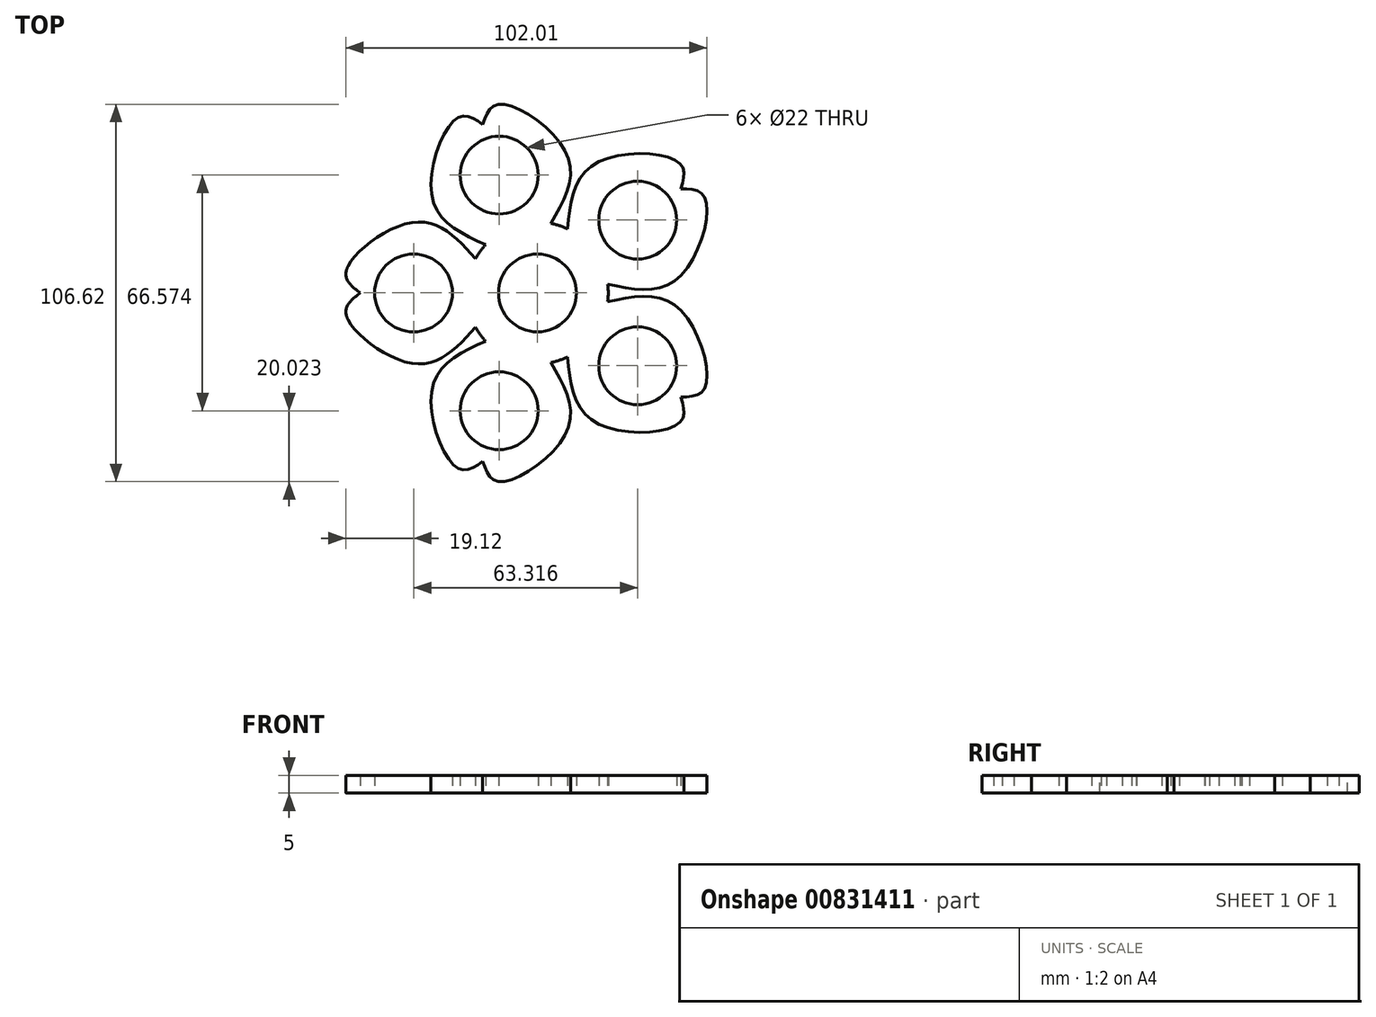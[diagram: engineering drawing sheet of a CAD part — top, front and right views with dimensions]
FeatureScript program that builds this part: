
annotation { "Feature Type Name" : "Feature", "Feature Type Description" : "" }
export const myFeature = defineFeature(function(context is Context, id is Id, definition is map)
    precondition{}
    {
        {
            var Q0;
            Q0=qCreatedBy(makeId("Top.planeOp"),FACE);
            var sketch = newSketch(context, id + "F0", { "sketchPlane" : qUnion([Q0])});
            skCircle(sketch, "E0", {"center": v(0, 0) * mm, "radius": 11 * mm});
            skArc(sketch, "E1", {"start": v(-17.5, -9.68) * mm, "mid": v(-16.18, -11.76) * mm, "end": v(-14.62, -13.65) * mm});
            skCircle(sketch, "E2", {"center": v(-35, 0) * mm, "radius": 11 * mm});
            skFitSpline(sketch, "E3", {"points": [v(-17.5, 9.68) * mm, v(-34.6, 20) * mm, v(-54.02, 6.18) * mm, v(-50.04, 0) * mm], "startDerivative": vector(-40.19, 44.56) * mm, "endDerivative": vector(30.5, -23.06) * mm});
            skArc(sketch, "E4.trimOffspring", {"start": v(-53.51, 7.57) * mm, "mid": v(-53.78, 6.88) * mm, "end": v(-54.02, 6.18) * mm});
            skFitSpline(sketch, "E5.MirrorCS", {"points": [v(-17.5, -9.68) * mm, v(-34.6, -20) * mm, v(-54.02, -6.18) * mm, v(-50.04, 0) * mm], "startDerivative": vector(-40.19, -44.56) * mm, "endDerivative": vector(30.5, 23.06) * mm});
            skArc(sketch, "E6.trimOffspring", {"start": v(-54.02, -6.18) * mm, "mid": v(-53.78, -6.88) * mm, "end": v(-53.51, -7.57) * mm});
            skCircle(sketch, "E7.1.0", {"center": v(-10.82, -33.29) * mm, "radius": 11 * mm});
            skCircle(sketch, "E7.2.0", {"center": v(28.32, -20.57) * mm, "radius": 11 * mm});
            skCircle(sketch, "E7.3.0", {"center": v(28.32, 20.57) * mm, "radius": 11 * mm});
            skCircle(sketch, "E7.4.0", {"center": v(-10.82, 33.29) * mm, "radius": 11 * mm});
            skFitSpline(sketch, "E8.MirrorCS", {"points": [v(-14.62, 13.65) * mm, v(-29.71, 26.73) * mm, v(-22.57, 49.46) * mm, v(-15.46, 47.6) * mm], "startDerivative": vector(-54.8, 24.45) * mm, "endDerivative": vector(31.35, -21.89) * mm});
            skFitSpline(sketch, "E9.MirrorCS", {"points": [v(3.8, 19.64) * mm, v(8.32, 39.1) * mm, v(-10.81, 53.29) * mm, v(-15.46, 47.6) * mm], "startDerivative": vector(29.96, 52) * mm, "endDerivative": vector(-12.5, -36.13) * mm});
            skFitSpline(sketch, "E10.MirrorCS", {"points": [v(8.47, 18.12) * mm, v(16.24, 36.52) * mm, v(40.07, 36.76) * mm, v(40.48, 29.41) * mm], "startDerivative": vector(6.32, 59.67) * mm, "endDerivative": vector(-11.13, -36.58) * mm});
            skFitSpline(sketch, "E11.MirrorCS", {"points": [v(19.85, 2.45) * mm, v(39.75, 4.16) * mm, v(47.34, 26.75) * mm, v(40.48, 29.41) * mm], "startDerivative": vector(58.7, -12.43) * mm, "endDerivative": vector(-38.23, 0.72) * mm});
            skFitSpline(sketch, "E12.MirrorCS", {"points": [v(19.85, -2.45) * mm, v(39.75, -4.16) * mm, v(47.34, -26.75) * mm, v(40.48, -29.41) * mm], "startDerivative": vector(58.7, 12.43) * mm, "endDerivative": vector(-38.23, -0.72) * mm});
            skFitSpline(sketch, "E13.MirrorCS", {"points": [v(8.47, -18.12) * mm, v(16.24, -36.52) * mm, v(40.07, -36.76) * mm, v(40.48, -29.41) * mm], "startDerivative": vector(6.32, -59.67) * mm, "endDerivative": vector(-11.13, 36.58) * mm});
            skFitSpline(sketch, "E14.MirrorCS", {"points": [v(3.8, -19.64) * mm, v(8.32, -39.1) * mm, v(-10.81, -53.29) * mm, v(-15.46, -47.6) * mm], "startDerivative": vector(29.96, -52) * mm, "endDerivative": vector(-12.5, 36.13) * mm});
            skFitSpline(sketch, "E15.MirrorCS", {"points": [v(-14.62, -13.65) * mm, v(-29.71, -26.73) * mm, v(-22.57, -49.46) * mm, v(-15.46, -47.6) * mm], "startDerivative": vector(-54.8, -24.45) * mm, "endDerivative": vector(31.35, 21.89) * mm});
            skArc(sketch, "E16.trimOffspring", {"start": v(3.8, -19.64) * mm, "mid": v(6.18, -19.02) * mm, "end": v(8.47, -18.12) * mm});
            skArc(sketch, "E17.trimOffspring", {"start": v(-14.62, 13.65) * mm, "mid": v(-16.18, 11.76) * mm, "end": v(-17.5, 9.68) * mm});
            skArc(sketch, "E18.trimOffspring", {"start": v(8.47, 18.12) * mm, "mid": v(6.18, 19.02) * mm, "end": v(3.8, 19.64) * mm});
            skArc(sketch, "E19.trimOffspring", {"start": v(19.85, -2.45) * mm, "mid": v(20, 0) * mm, "end": v(19.85, 2.45) * mm});
            skSolve(sketch);
        }
        {
            var Q0;
            Q0=makeQuery(id+"F0.imprint","IMPRINT",FACE,{"disambiguationData":[TD([[makeQuery(id+"F0.imprint","IMPRINT",EDGE,{"derivedFrom":sQuery(id+"F0.wireOp",EDGE,"E0")}),-1.0]])]});
            var Q1;
            {var subQ0=sQuery(id+"F0.wireOp",EDGE,"E4.trimOffspring");Q1=makeQuery(id+"F0.imprint","IMPRINT",FACE,{"disambiguationData":[TD([[makeQuery(id+"F0.imprint","IMPRINT",EDGE,{"derivedFrom":subQ0}),-1.0]])]});}
            var Q2;
            {var subQ0=sQuery(id+"F0.wireOp",EDGE,"E6.trimOffspring");Q2=makeQuery(id+"F0.imprint","IMPRINT",FACE,{"disambiguationData":[TD([[makeQuery(id+"F0.imprint","IMPRINT",EDGE,{"derivedFrom":subQ0}),-1.0]])]});}
            extrude(context, id + "F1", {"entities" : qUnion([Q0, Q1, Q2]), "depth" : 5 * mm, "offsetDistance" : 25 * mm});
        }
    });
